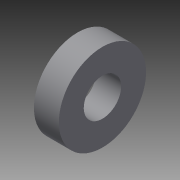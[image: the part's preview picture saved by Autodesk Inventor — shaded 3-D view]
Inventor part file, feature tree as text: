
AUTODESK INVENTOR PART (.ipt)
format: ipt  version: 2015 (Build 190159000, 159)  size: 79,360 bytes
history: native  units: in
note: dims shown in document units (in); Inventor stores cm internally (conversion verified against a paired STEP export)
features: extrude x1, sketch x1
ambient origin geometry x8: Origin, YZ Plane, XZ Plane, XY Plane, X Axis, Y Axis, Z Axis, Center Point
bodies: Solid1 (feature_tree)
feature tree (2):
  extrude  "Extrusion1"  Depth=0.2812in
  sketch  "Sketch1"  dims[d0=0.875in d1=0.375in d2=0.2812in d3=0.0in]
